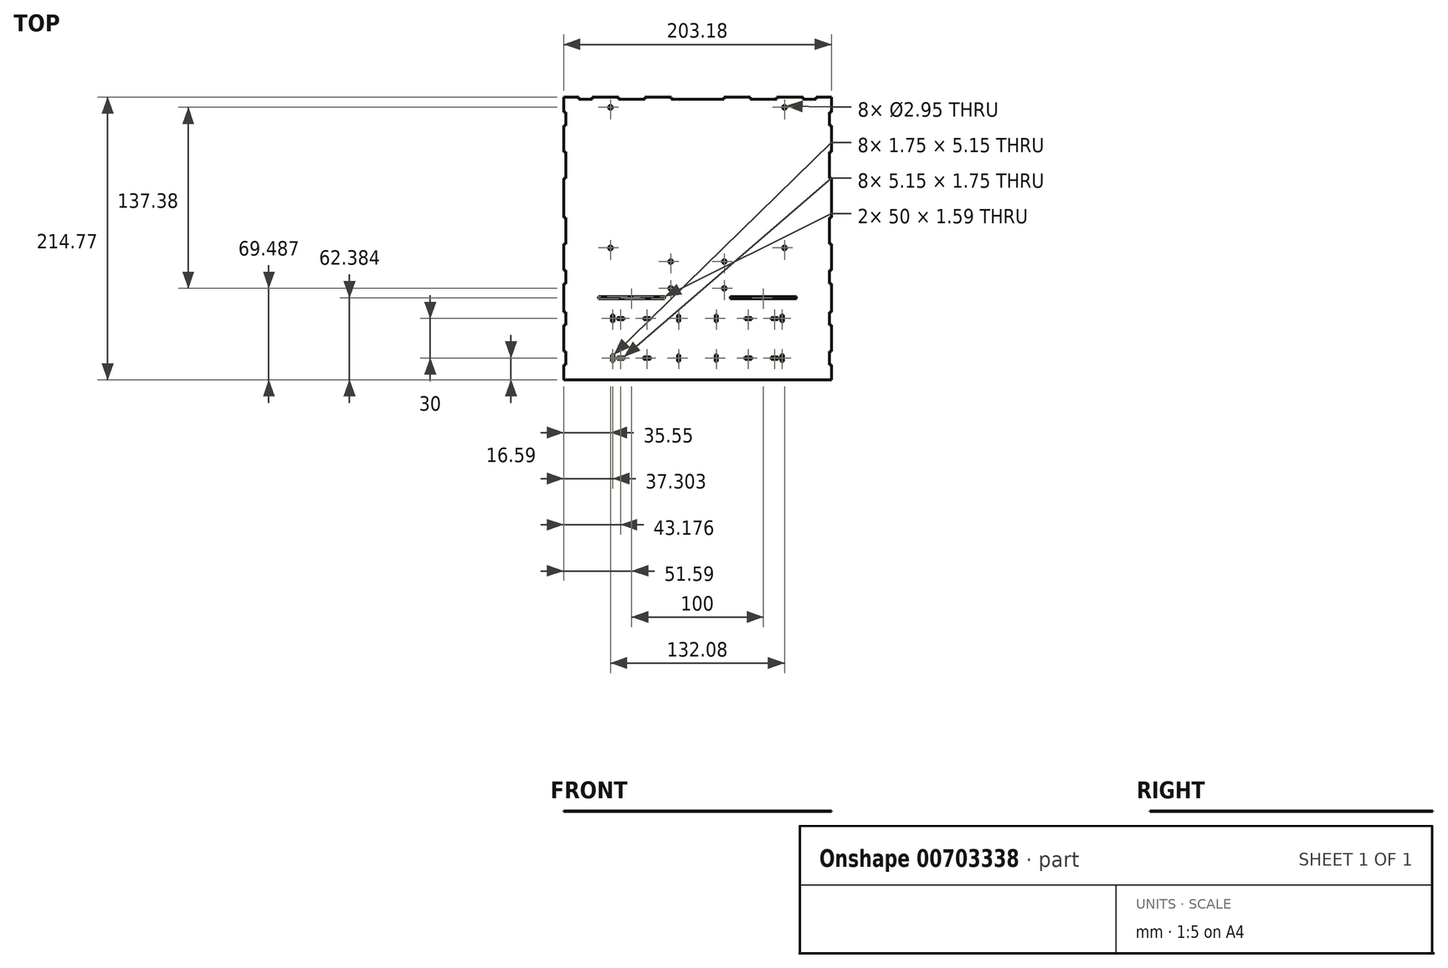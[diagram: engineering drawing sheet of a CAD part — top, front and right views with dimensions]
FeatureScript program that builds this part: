
annotation { "Feature Type Name" : "Feature", "Feature Type Description" : "" }
export const myFeature = defineFeature(function(context is Context, id is Id, definition is map)
    precondition{}
    {
        {
            var Q0;
            Q0=qCreatedBy(makeId("Top.planeOp"),FACE);
            var sketch = newSketch(context, id + "F0", { "sketchPlane" : qUnion([Q0])});
            skLineSegment(sketch, "E0.bottom", {"start": v(100, 20) * mm, "end": v(-100, 20) * mm});
            skLineSegment(sketch, "E0.top", {"start": v(100, -20) * mm, "end": v(-100, -20) * mm});
            skLineSegment(sketch, "E0.left", {"start": v(100, 20) * mm, "end": v(100, -20) * mm});
            skLineSegment(sketch, "E0.right", {"start": v(-100, 20) * mm, "end": v(-100, -20) * mm});
            skPoint(sketch, "E0.middle", {"position": v(0, 0) * mm});
            skLineSegment(sketch, "E1.bottom", {"start": v(-13.41, 12.42) * mm, "end": v(-15.16, 12.42) * mm});
            skLineSegment(sketch, "E1.top", {"start": v(-13.41, 17.57) * mm, "end": v(-15.16, 17.57) * mm});
            skLineSegment(sketch, "E1.left", {"start": v(-13.41, 12.42) * mm, "end": v(-13.41, 17.57) * mm});
            skLineSegment(sketch, "E1.right", {"start": v(-15.16, 12.42) * mm, "end": v(-15.16, 17.57) * mm});
            skPoint(sketch, "E1.middle", {"position": v(-14.29, 15) * mm});
            skPoint(sketch, "E2.cornerSnap0", {"position": v(-13.41, 15) * mm});
            skLineSegment(sketch, "E3.bottom", {"start": v(15.16, 12.42) * mm, "end": v(13.41, 12.42) * mm});
            skLineSegment(sketch, "E3.top", {"start": v(15.16, 17.57) * mm, "end": v(13.41, 17.57) * mm});
            skLineSegment(sketch, "E3.left", {"start": v(15.16, 12.42) * mm, "end": v(15.16, 17.57) * mm});
            skLineSegment(sketch, "E3.right", {"start": v(13.41, 12.42) * mm, "end": v(13.41, 17.57) * mm});
            skPoint(sketch, "E3.middle", {"position": v(14.29, 15) * mm});
            skLineSegment(sketch, "E4.bottom", {"start": v(15.16, -12.43) * mm, "end": v(13.41, -12.43) * mm});
            skLineSegment(sketch, "E4.top", {"start": v(15.16, -17.57) * mm, "end": v(13.41, -17.57) * mm});
            skLineSegment(sketch, "E4.left", {"start": v(15.16, -12.43) * mm, "end": v(15.16, -17.57) * mm});
            skLineSegment(sketch, "E4.right", {"start": v(13.41, -12.43) * mm, "end": v(13.41, -17.57) * mm});
            skPoint(sketch, "E4.middle", {"position": v(14.29, -15) * mm});
            skLineSegment(sketch, "E5.bottom", {"start": v(-13.41, -12.43) * mm, "end": v(-15.16, -12.43) * mm});
            skLineSegment(sketch, "E5.top", {"start": v(-13.41, -17.57) * mm, "end": v(-15.16, -17.57) * mm});
            skLineSegment(sketch, "E5.left", {"start": v(-13.41, -12.43) * mm, "end": v(-13.41, -17.57) * mm});
            skLineSegment(sketch, "E5.right", {"start": v(-15.16, -12.43) * mm, "end": v(-15.16, -17.57) * mm});
            skPoint(sketch, "E5.middle", {"position": v(-14.29, -15) * mm});
            skLineSegment(sketch, "E6.bottom", {"start": v(-63.41, 12.42) * mm, "end": v(-65.16, 12.42) * mm});
            skLineSegment(sketch, "E6.top", {"start": v(-63.41, 17.57) * mm, "end": v(-65.16, 17.57) * mm});
            skLineSegment(sketch, "E6.left", {"start": v(-63.41, 12.42) * mm, "end": v(-63.41, 17.57) * mm});
            skLineSegment(sketch, "E6.right", {"start": v(-65.16, 12.42) * mm, "end": v(-65.16, 17.57) * mm});
            skPoint(sketch, "E6.middle", {"position": v(-64.29, 15) * mm});
            skPoint(sketch, "E7.cornerSnap0", {"position": v(-63.41, 15) * mm});
            skLineSegment(sketch, "E8.bottom", {"start": v(-63.41, -17.57) * mm, "end": v(-65.16, -17.57) * mm});
            skLineSegment(sketch, "E8.top", {"start": v(-63.41, -12.42) * mm, "end": v(-65.16, -12.42) * mm});
            skLineSegment(sketch, "E8.left", {"start": v(-63.41, -17.58) * mm, "end": v(-63.41, -12.43) * mm});
            skLineSegment(sketch, "E8.right", {"start": v(-65.16, -17.58) * mm, "end": v(-65.16, -12.43) * mm});
            skPoint(sketch, "E8.middle", {"position": v(-64.29, -15) * mm});
            skPoint(sketch, "E9.cornerSnap0", {"position": v(-63.41, -15) * mm});
            skLineSegment(sketch, "E10.bottom", {"start": v(65.16, -17.57) * mm, "end": v(63.41, -17.57) * mm});
            skLineSegment(sketch, "E10.top", {"start": v(65.16, -12.43) * mm, "end": v(63.41, -12.43) * mm});
            skLineSegment(sketch, "E10.left", {"start": v(65.16, -17.58) * mm, "end": v(65.16, -12.43) * mm});
            skLineSegment(sketch, "E10.right", {"start": v(63.41, -17.58) * mm, "end": v(63.41, -12.43) * mm});
            skPoint(sketch, "E10.middle", {"position": v(64.29, -15) * mm});
            skPoint(sketch, "E11.cornerSnap0", {"position": v(65.16, -15) * mm});
            skLineSegment(sketch, "E12.bottom", {"start": v(65.16, 12.43) * mm, "end": v(63.41, 12.43) * mm});
            skLineSegment(sketch, "E12.top", {"start": v(65.16, 17.57) * mm, "end": v(63.41, 17.57) * mm});
            skLineSegment(sketch, "E12.left", {"start": v(65.16, 12.43) * mm, "end": v(65.16, 17.58) * mm});
            skLineSegment(sketch, "E12.right", {"start": v(63.41, 12.43) * mm, "end": v(63.41, 17.57) * mm});
            skPoint(sketch, "E12.middle", {"position": v(64.29, 15) * mm});
            skPoint(sketch, "E13.cornerSnap0", {"position": v(65.16, 15) * mm});
            skLineSegment(sketch, "E14.bottom", {"start": v(-55.84, -15.87) * mm, "end": v(-60.99, -15.87) * mm});
            skLineSegment(sketch, "E14.top", {"start": v(-55.84, -14.13) * mm, "end": v(-60.99, -14.13) * mm});
            skLineSegment(sketch, "E14.left", {"start": v(-55.84, -15.87) * mm, "end": v(-55.84, -14.13) * mm});
            skLineSegment(sketch, "E14.right", {"start": v(-60.99, -15.87) * mm, "end": v(-60.99, -14.13) * mm});
            skPoint(sketch, "E14.middle", {"position": v(-58.41, -15) * mm});
            skLineSegment(sketch, "E15.bottom", {"start": v(60.99, -15.87) * mm, "end": v(55.84, -15.87) * mm});
            skLineSegment(sketch, "E15.top", {"start": v(60.99, -14.13) * mm, "end": v(55.84, -14.13) * mm});
            skLineSegment(sketch, "E15.left", {"start": v(60.99, -15.87) * mm, "end": v(60.99, -14.13) * mm});
            skLineSegment(sketch, "E15.right", {"start": v(55.84, -15.87) * mm, "end": v(55.84, -14.13) * mm});
            skPoint(sketch, "E15.middle", {"position": v(58.41, -15) * mm});
            skLineSegment(sketch, "E16.bottom", {"start": v(60.99, 14.13) * mm, "end": v(55.84, 14.13) * mm});
            skLineSegment(sketch, "E16.top", {"start": v(60.99, 15.87) * mm, "end": v(55.84, 15.87) * mm});
            skLineSegment(sketch, "E16.left", {"start": v(60.99, 14.13) * mm, "end": v(60.99, 15.87) * mm});
            skLineSegment(sketch, "E16.right", {"start": v(55.84, 14.13) * mm, "end": v(55.84, 15.87) * mm});
            skPoint(sketch, "E16.middle", {"position": v(58.41, 15) * mm});
            skLineSegment(sketch, "E17.bottom", {"start": v(-55.84, 14.13) * mm, "end": v(-60.99, 14.13) * mm});
            skLineSegment(sketch, "E17.top", {"start": v(-55.84, 15.87) * mm, "end": v(-60.99, 15.87) * mm});
            skLineSegment(sketch, "E17.left", {"start": v(-55.84, 14.13) * mm, "end": v(-55.84, 15.87) * mm});
            skLineSegment(sketch, "E17.right", {"start": v(-60.99, 14.13) * mm, "end": v(-60.99, 15.87) * mm});
            skPoint(sketch, "E17.middle", {"position": v(-58.41, 15) * mm});
            skLineSegment(sketch, "E18.bottom", {"start": v(-35.84, 14.13) * mm, "end": v(-40.99, 14.13) * mm});
            skLineSegment(sketch, "E18.top", {"start": v(-35.84, 15.87) * mm, "end": v(-40.99, 15.87) * mm});
            skLineSegment(sketch, "E18.left", {"start": v(-35.84, 14.13) * mm, "end": v(-35.84, 15.87) * mm});
            skLineSegment(sketch, "E18.right", {"start": v(-40.99, 14.13) * mm, "end": v(-40.99, 15.87) * mm});
            skPoint(sketch, "E18.middle", {"position": v(-38.41, 15) * mm});
            skLineSegment(sketch, "E19.bottom", {"start": v(40.99, 14.13) * mm, "end": v(35.84, 14.13) * mm});
            skLineSegment(sketch, "E19.top", {"start": v(40.99, 15.87) * mm, "end": v(35.84, 15.87) * mm});
            skLineSegment(sketch, "E19.left", {"start": v(40.99, 14.13) * mm, "end": v(40.99, 15.87) * mm});
            skLineSegment(sketch, "E19.right", {"start": v(35.84, 14.13) * mm, "end": v(35.84, 15.87) * mm});
            skPoint(sketch, "E19.middle", {"position": v(38.41, 15) * mm});
            skLineSegment(sketch, "E20.bottom", {"start": v(-35.84, -15.87) * mm, "end": v(-40.99, -15.87) * mm});
            skLineSegment(sketch, "E20.top", {"start": v(-35.84, -14.13) * mm, "end": v(-40.99, -14.13) * mm});
            skLineSegment(sketch, "E20.left", {"start": v(-35.84, -15.87) * mm, "end": v(-35.84, -14.13) * mm});
            skLineSegment(sketch, "E20.right", {"start": v(-40.99, -15.87) * mm, "end": v(-40.99, -14.13) * mm});
            skPoint(sketch, "E20.middle", {"position": v(-38.41, -15) * mm});
            skLineSegment(sketch, "E21.bottom", {"start": v(40.99, -15.87) * mm, "end": v(35.84, -15.87) * mm});
            skLineSegment(sketch, "E21.top", {"start": v(40.99, -14.13) * mm, "end": v(35.84, -14.13) * mm});
            skLineSegment(sketch, "E21.left", {"start": v(40.99, -15.87) * mm, "end": v(40.99, -14.13) * mm});
            skLineSegment(sketch, "E21.right", {"start": v(35.84, -15.87) * mm, "end": v(35.84, -14.13) * mm});
            skPoint(sketch, "E21.middle", {"position": v(38.41, -15) * mm});
            skLineSegment(sketch, "E22", {"start": v(100, 20) * mm, "end": v(100, 30) * mm});
            skLineSegment(sketch, "E23", {"start": v(100, 30) * mm, "end": v(-100, 30) * mm});
            skLineSegment(sketch, "E24", {"start": v(-100, 30) * mm, "end": v(-100, 20) * mm});
            skLineSegment(sketch, "E25", {"start": v(-100, -20) * mm, "end": v(-100, -30) * mm});
            skLineSegment(sketch, "E26", {"start": v(-100, -30) * mm, "end": v(100, -30) * mm});
            skLineSegment(sketch, "E27", {"start": v(100, -30) * mm, "end": v(100, -20) * mm});
            skLineSegment(sketch, "E28", {"start": v(-100, 10) * mm, "end": v(-101.59, 10) * mm});
            skLineSegment(sketch, "E29", {"start": v(-101.59, 10) * mm, "end": v(-101.59, -10) * mm});
            skLineSegment(sketch, "E30", {"start": v(-101.59, -10) * mm, "end": v(-100, -10) * mm});
            skLineSegment(sketch, "E31", {"start": v(100, 10) * mm, "end": v(101.59, 10) * mm});
            skLineSegment(sketch, "E32", {"start": v(101.59, 10) * mm, "end": v(101.59, -10) * mm});
            skLineSegment(sketch, "E33", {"start": v(101.59, -10) * mm, "end": v(100, -10) * mm});
            skLineSegment(sketch, "E34", {"start": v(-100, 20) * mm, "end": v(-101.59, 20) * mm});
            skLineSegment(sketch, "E35", {"start": v(-101.59, 20) * mm, "end": v(-101.59, 30) * mm});
            skLineSegment(sketch, "E36", {"start": v(-101.59, 30) * mm, "end": v(-100, 30) * mm});
            skLineSegment(sketch, "E37", {"start": v(-100, -20) * mm, "end": v(-101.59, -20) * mm});
            skLineSegment(sketch, "E38", {"start": v(-101.59, -20) * mm, "end": v(-101.59, -30) * mm});
            skLineSegment(sketch, "E39", {"start": v(-101.59, -30) * mm, "end": v(-100, -30) * mm});
            skLineSegment(sketch, "E40", {"start": v(100, -20) * mm, "end": v(101.59, -20) * mm});
            skLineSegment(sketch, "E41", {"start": v(101.59, -20) * mm, "end": v(101.59, -30) * mm});
            skLineSegment(sketch, "E42", {"start": v(101.59, -30) * mm, "end": v(100, -30) * mm});
            skLineSegment(sketch, "E43", {"start": v(100, 30) * mm, "end": v(101.59, 30) * mm});
            skLineSegment(sketch, "E44", {"start": v(101.59, 30) * mm, "end": v(101.59, 20) * mm});
            skLineSegment(sketch, "E45", {"start": v(101.59, 20) * mm, "end": v(100, 20) * mm});
            skLineSegment(sketch, "E46", {"start": v(-101.59, 30) * mm, "end": v(-101.59, 31.59) * mm});
            skLineSegment(sketch, "E47", {"start": v(-101.59, 31.59) * mm, "end": v(101.59, 31.59) * mm});
            skLineSegment(sketch, "E48", {"start": v(101.59, 31.59) * mm, "end": v(101.59, 30) * mm});
            skLineSegment(sketch, "E49", {"start": v(101.59, -30) * mm, "end": v(101.59, -31.59) * mm});
            skLineSegment(sketch, "E50", {"start": v(101.59, -31.59) * mm, "end": v(-100, -31.59) * mm});
            skLineSegment(sketch, "E51", {"start": v(-100, -31.59) * mm, "end": v(-100, -30) * mm});
            skLineSegment(sketch, "E52", {"start": v(-75, 31.59) * mm, "end": v(-75, 30) * mm});
            skLineSegment(sketch, "E53", {"start": v(-25, 31.59) * mm, "end": v(-25, 30) * mm});
            skLineSegment(sketch, "E54", {"start": v(25, 31.59) * mm, "end": v(25, 30) * mm});
            skLineSegment(sketch, "E55", {"start": v(75, 31.59) * mm, "end": v(75, 30) * mm});
            skLineSegment(sketch, "E56", {"start": v(-101.59, -30) * mm, "end": v(-101.59, -31.59) * mm});
            skLineSegment(sketch, "E57", {"start": v(-101.59, -31.59) * mm, "end": v(-100, -31.59) * mm});
            skLineSegment(sketch, "E58", {"start": v(-101.59, 31.59) * mm, "end": v(-101.59, 181.59) * mm});
            skLineSegment(sketch, "E59", {"start": v(-101.59, 181.59) * mm, "end": v(101.59, 181.59) * mm});
            skLineSegment(sketch, "E60", {"start": v(101.59, 181.59) * mm, "end": v(101.59, 31.59) * mm});
            skLineSegment(sketch, "E61", {"start": v(-100, 30) * mm, "end": v(-100, 181.59) * mm});
            skLineSegment(sketch, "E62", {"start": v(100, 30) * mm, "end": v(100, 181.59) * mm});
            skLineSegment(sketch, "E63", {"start": v(101.59, 41.59) * mm, "end": v(100, 41.59) * mm});
            skLineSegment(sketch, "E64", {"start": v(100, 51.59) * mm, "end": v(101.59, 51.59) * mm});
            skLineSegment(sketch, "E65", {"start": v(101.59, 171.59) * mm, "end": v(100, 171.59) * mm});
            skLineSegment(sketch, "E66", {"start": v(101.59, 161.59) * mm, "end": v(100, 161.59) * mm});
            skLineSegment(sketch, "E67", {"start": v(-100, 41.59) * mm, "end": v(-101.59, 41.59) * mm});
            skLineSegment(sketch, "E68", {"start": v(-100, 51.59) * mm, "end": v(-101.59, 51.59) * mm});
            skLineSegment(sketch, "E69", {"start": v(-100, 171.59) * mm, "end": v(-101.59, 171.59) * mm});
            skLineSegment(sketch, "E70", {"start": v(-100, 161.59) * mm, "end": v(-101.59, 161.59) * mm});
            skLineSegment(sketch, "E71", {"start": v(101.59, 141.59) * mm, "end": v(100, 141.59) * mm});
            skLineSegment(sketch, "E72", {"start": v(101.59, 121.59) * mm, "end": v(100, 121.59) * mm});
            skLineSegment(sketch, "E73", {"start": v(101.59, 71.59) * mm, "end": v(100, 71.59) * mm});
            skLineSegment(sketch, "E74", {"start": v(101.59, 91.59) * mm, "end": v(100, 91.59) * mm});
            skLineSegment(sketch, "E75", {"start": v(-100, 141.59) * mm, "end": v(-101.59, 141.59) * mm});
            skLineSegment(sketch, "E76", {"start": v(-100, 121.59) * mm, "end": v(-101.59, 121.59) * mm});
            skLineSegment(sketch, "E77", {"start": v(-100, 71.59) * mm, "end": v(-101.59, 71.59) * mm});
            skLineSegment(sketch, "E78", {"start": v(-100, 91.59) * mm, "end": v(-101.59, 91.59) * mm});
            skCircle(sketch, "E79", {"center": v(-66.04, 175.28) * mm, "radius": 1.47 * mm});
            skCircle(sketch, "E80", {"center": v(66.04, 175.28) * mm, "radius": 1.47 * mm});
            skCircle(sketch, "E81", {"center": v(-66.04, 68.6) * mm, "radius": 1.47 * mm});
            skCircle(sketch, "E82", {"center": v(66.04, 68.6) * mm, "radius": 1.47 * mm});
            skLineSegment(sketch, "E83", {"start": v(-101.59, 181.59) * mm, "end": v(-101.59, 183.18) * mm});
            skLineSegment(sketch, "E84", {"start": v(-101.59, 183.18) * mm, "end": v(101.59, 183.18) * mm});
            skLineSegment(sketch, "E85", {"start": v(101.59, 183.18) * mm, "end": v(101.59, 181.59) * mm});
            skLineSegment(sketch, "E86", {"start": v(100, 181.59) * mm, "end": v(100, 183.18) * mm});
            skLineSegment(sketch, "E87", {"start": v(-100, 181.59) * mm, "end": v(-100, 183.18) * mm});
            skLineSegment(sketch, "E88", {"start": v(-90, 181.59) * mm, "end": v(-90, 183.18) * mm});
            skLineSegment(sketch, "E89", {"start": v(-80, 183.17) * mm, "end": v(-80, 181.59) * mm});
            skLineSegment(sketch, "E90", {"start": v(-60, 181.59) * mm, "end": v(-60, 183.17) * mm});
            skLineSegment(sketch, "E91", {"start": v(-40, 181.59) * mm, "end": v(-40, 183.17) * mm});
            skLineSegment(sketch, "E92", {"start": v(90, 183.18) * mm, "end": v(90, 181.59) * mm});
            skLineSegment(sketch, "E93", {"start": v(80, 183.18) * mm, "end": v(80, 181.59) * mm});
            skLineSegment(sketch, "E94", {"start": v(60, 183.18) * mm, "end": v(60, 181.59) * mm});
            skLineSegment(sketch, "E95", {"start": v(40, 183.18) * mm, "end": v(40, 181.59) * mm});
            skLineSegment(sketch, "E96", {"start": v(-20, 183.18) * mm, "end": v(-20, 181.59) * mm});
            skLineSegment(sketch, "E97", {"start": v(20, 183.18) * mm, "end": v(20, 181.59) * mm});
            skCircle(sketch, "E98", {"center": v(20.32, 58.22) * mm, "radius": 1.47 * mm});
            skCircle(sketch, "E99", {"center": v(20.32, 37.9) * mm, "radius": 1.47 * mm});
            skCircle(sketch, "E100", {"center": v(-20.32, 37.9) * mm, "radius": 1.47 * mm});
            skCircle(sketch, "E101", {"center": v(-20.32, 58.22) * mm, "radius": 1.47 * mm});
            skSolve(sketch);
        }
        {
            var Q0;
            {var subQ3=sQuery(id+"F0.wireOp",EDGE,"E69");Q0=makeQuery(id+"F0.imprint","IMPRINT",FACE,{"disambiguationData":[TD([[makeQuery(id+"F0.imprint","IMPRINT",EDGE,{"derivedFrom":subQ3}),-1.0]])]});}
            var Q1;
            {var subQ5=sQuery(id+"F0.wireOp",EDGE,"E67");Q1=makeQuery(id+"F0.imprint","IMPRINT",FACE,{"disambiguationData":[TD([[makeQuery(id+"F0.imprint","IMPRINT",EDGE,{"derivedFrom":subQ5}),1.0]])]});}
            var Q2;
            {var subQ0=sQuery(id+"F0.wireOp",EDGE,"E68");Q2=makeQuery(id+"F0.imprint","IMPRINT",FACE,{"disambiguationData":[TD([[makeQuery(id+"F0.imprint","IMPRINT",EDGE,{"derivedFrom":subQ0}),-1.0]])]});}
            var Q3;
            {var subQ5=sQuery(id+"F0.wireOp",EDGE,"E65");Q3=makeQuery(id+"F0.imprint","IMPRINT",FACE,{"disambiguationData":[TD([[makeQuery(id+"F0.imprint","IMPRINT",EDGE,{"derivedFrom":subQ5}),-1.0]])]});}
            var Q4;
            {var subQ5=sQuery(id+"F0.wireOp",EDGE,"E63");Q4=makeQuery(id+"F0.imprint","IMPRINT",FACE,{"disambiguationData":[TD([[makeQuery(id+"F0.imprint","IMPRINT",EDGE,{"derivedFrom":subQ5}),1.0]])]});}
            var Q5;
            {var subQ0=sQuery(id+"F0.wireOp",EDGE,"E64");Q5=makeQuery(id+"F0.imprint","IMPRINT",FACE,{"disambiguationData":[TD([[makeQuery(id+"F0.imprint","IMPRINT",EDGE,{"derivedFrom":subQ0}),1.0]])]});}
            var Q6;
            {var subQ4=sQuery(id+"F0.wireOp",EDGE,"E0.bottom");Q6=makeQuery(id+"F0.imprint","IMPRINT",FACE,{"disambiguationData":[TD([[makeQuery(id+"F0.imprint","IMPRINT",EDGE,{"derivedFrom":subQ4}),1.0]])]});}
            var Q7;
            Q7=makeQuery(id+"F0.imprint","IMPRINT",FACE,{"disambiguationData":[TD([[makeQuery(id+"F0.imprint","IMPRINT",EDGE,{"derivedFrom":sQuery(id+"F0.wireOp",EDGE,"E0.bottom")}),-1.0]])]});
            var Q8;
            Q8=makeQuery(id+"F0.imprint","IMPRINT",FACE,{"disambiguationData":[TD([[makeQuery(id+"F0.imprint","IMPRINT",EDGE,{"derivedFrom":sQuery(id+"F0.wireOp",EDGE,"E0.top")}),1.0]])]});
            var Q9;
            {var subQ0=sQuery(id+"F0.wireOp",EDGE,"E28");Q9=makeQuery(id+"F0.imprint","IMPRINT",FACE,{"disambiguationData":[TD([[makeQuery(id+"F0.imprint","IMPRINT",EDGE,{"derivedFrom":subQ0}),1.0]])]});}
            var Q10;
            {var subQ0=sQuery(id+"F0.wireOp",EDGE,"E31");Q10=makeQuery(id+"F0.imprint","IMPRINT",FACE,{"disambiguationData":[TD([[makeQuery(id+"F0.imprint","IMPRINT",EDGE,{"derivedFrom":subQ0}),-1.0]])]});}
            var Q11;
            Q11=makeQuery(id+"F0.imprint","IMPRINT",FACE,{"disambiguationData":[TD([[makeQuery(id+"F0.imprint","IMPRINT",EDGE,{"derivedFrom":sQuery(id+"F0.wireOp",EDGE,"E22")}),-1.0]])]});
            var Q12;
            Q12=makeQuery(id+"F0.imprint","IMPRINT",FACE,{"disambiguationData":[TD([[makeQuery(id+"F0.imprint","IMPRINT",EDGE,{"derivedFrom":sQuery(id+"F0.wireOp",EDGE,"E27")}),-1.0]])]});
            var Q13;
            Q13=makeQuery(id+"F0.imprint","IMPRINT",FACE,{"disambiguationData":[TD([[makeQuery(id+"F0.imprint","IMPRINT",EDGE,{"derivedFrom":sQuery(id+"F0.wireOp",EDGE,"E24")}),-1.0]])]});
            var Q14;
            Q14=makeQuery(id+"F0.imprint","IMPRINT",FACE,{"disambiguationData":[TD([[makeQuery(id+"F0.imprint","IMPRINT",EDGE,{"derivedFrom":sQuery(id+"F0.wireOp",EDGE,"E25")}),-1.0]])]});
            var Q15;
            Q15=makeQuery(id+"F0.imprint","IMPRINT",FACE,{"disambiguationData":[TD([[makeQuery(id+"F0.imprint","IMPRINT",EDGE,{"derivedFrom":sQuery(id+"F0.wireOp",EDGE,"E26")}),-1.0]])]});
            var Q16;
            {var subQ0=sQuery(id+"F0.wireOp",EDGE,"E36");Q16=makeQuery(id+"F0.imprint","IMPRINT",FACE,{"disambiguationData":[TD([[makeQuery(id+"F0.imprint","IMPRINT",EDGE,{"derivedFrom":subQ0}),1.0]])]});}
            var Q17;
            {var subQ0=sQuery(id+"F0.wireOp",EDGE,"E53");Q17=makeQuery(id+"F0.imprint","IMPRINT",FACE,{"disambiguationData":[TD([[makeQuery(id+"F0.imprint","IMPRINT",EDGE,{"derivedFrom":subQ0}),1.0]])]});}
            var Q18;
            {var subQ0=sQuery(id+"F0.wireOp",EDGE,"E43");Q18=makeQuery(id+"F0.imprint","IMPRINT",FACE,{"disambiguationData":[TD([[makeQuery(id+"F0.imprint","IMPRINT",EDGE,{"derivedFrom":subQ0}),1.0]])]});}
            var Q19;
            Q19=makeQuery(id+"F0.imprint","IMPRINT",FACE,{"disambiguationData":[TD([[makeQuery(id+"F0.imprint","IMPRINT",EDGE,{"derivedFrom":sQuery(id+"F0.wireOp",EDGE,"E39")}),-1.0]])]});
            var Q20;
            {var subQ4=sQuery(id+"F0.wireOp",EDGE,"E47");var subQ13=makeQuery(id+"F0.imprint","INTERSECT",VERTEX,{"derivedFrom":[subQ4,sQuery(id+"F0.wireOp",EDGE,"E52")]});Q20=makeQuery(id+"F0.imprint","IMPRINT",FACE,{"disambiguationData":[TD([[makeQuery(id+"F0.imprint","IMPRINT",EDGE,{"disambiguationData":[TD([[subQ13,1.0]])],"derivedFrom":subQ4}),1.0]])]});}
            var Q21;
            {var subQ3=sQuery(id+"F0.wireOp",EDGE,"E55");Q21=makeQuery(id+"F0.imprint","IMPRINT",FACE,{"disambiguationData":[TD([[makeQuery(id+"F0.imprint","IMPRINT",EDGE,{"derivedFrom":subQ3}),1.0]])]});}
            var Q22;
            {var subQ3=sQuery(id+"F0.wireOp",EDGE,"E52");Q22=makeQuery(id+"F0.imprint","IMPRINT",FACE,{"disambiguationData":[TD([[makeQuery(id+"F0.imprint","IMPRINT",EDGE,{"derivedFrom":subQ3}),-1.0]])]});}
            var Q23;
            {var subQ0=sQuery(id+"F0.wireOp",EDGE,"E76");Q23=makeQuery(id+"F0.imprint","IMPRINT",FACE,{"disambiguationData":[TD([[makeQuery(id+"F0.imprint","IMPRINT",EDGE,{"derivedFrom":subQ0}),1.0]])]});}
            var Q24;
            {var subQ0=sQuery(id+"F0.wireOp",EDGE,"E70");Q24=makeQuery(id+"F0.imprint","IMPRINT",FACE,{"disambiguationData":[TD([[makeQuery(id+"F0.imprint","IMPRINT",EDGE,{"derivedFrom":subQ0}),1.0]])]});}
            var Q25;
            {var subQ0=sQuery(id+"F0.wireOp",EDGE,"E66");Q25=makeQuery(id+"F0.imprint","IMPRINT",FACE,{"disambiguationData":[TD([[makeQuery(id+"F0.imprint","IMPRINT",EDGE,{"derivedFrom":subQ0}),1.0]])]});}
            var Q26;
            {var subQ0=sQuery(id+"F0.wireOp",EDGE,"E72");Q26=makeQuery(id+"F0.imprint","IMPRINT",FACE,{"disambiguationData":[TD([[makeQuery(id+"F0.imprint","IMPRINT",EDGE,{"derivedFrom":subQ0}),1.0]])]});}
            var Q27;
            {var subQ2=sQuery(id+"F0.wireOp",EDGE,"E86");Q27=makeQuery(id+"F0.imprint","IMPRINT",FACE,{"disambiguationData":[TD([[makeQuery(id+"F0.imprint","IMPRINT",EDGE,{"derivedFrom":subQ2}),1.0]])]});}
            var Q28;
            {var subQ0=sQuery(id+"F0.wireOp",EDGE,"E85");Q28=makeQuery(id+"F0.imprint","IMPRINT",FACE,{"disambiguationData":[TD([[makeQuery(id+"F0.imprint","IMPRINT",EDGE,{"derivedFrom":subQ0}),-1.0]])]});}
            var Q29;
            {var subQ0=sQuery(id+"F0.wireOp",EDGE,"E83");Q29=makeQuery(id+"F0.imprint","IMPRINT",FACE,{"disambiguationData":[TD([[makeQuery(id+"F0.imprint","IMPRINT",EDGE,{"derivedFrom":subQ0}),-1.0]])]});}
            var Q30;
            {var subQ0=sQuery(id+"F0.wireOp",EDGE,"E87");Q30=makeQuery(id+"F0.imprint","IMPRINT",FACE,{"disambiguationData":[TD([[makeQuery(id+"F0.imprint","IMPRINT",EDGE,{"derivedFrom":subQ0}),-1.0]])]});}
            var Q31;
            {var subQ0=sQuery(id+"F0.wireOp",EDGE,"E89");Q31=makeQuery(id+"F0.imprint","IMPRINT",FACE,{"disambiguationData":[TD([[makeQuery(id+"F0.imprint","IMPRINT",EDGE,{"derivedFrom":subQ0}),1.0]])]});}
            var Q32;
            {var subQ0=sQuery(id+"F0.wireOp",EDGE,"E91");Q32=makeQuery(id+"F0.imprint","IMPRINT",FACE,{"disambiguationData":[TD([[makeQuery(id+"F0.imprint","IMPRINT",EDGE,{"derivedFrom":subQ0}),-1.0]])]});}
            var Q33;
            {var subQ0=sQuery(id+"F0.wireOp",EDGE,"E93");Q33=makeQuery(id+"F0.imprint","IMPRINT",FACE,{"disambiguationData":[TD([[makeQuery(id+"F0.imprint","IMPRINT",EDGE,{"derivedFrom":subQ0}),-1.0]])]});}
            var Q34;
            {var subQ0=sQuery(id+"F0.wireOp",EDGE,"E95");Q34=makeQuery(id+"F0.imprint","IMPRINT",FACE,{"disambiguationData":[TD([[makeQuery(id+"F0.imprint","IMPRINT",EDGE,{"derivedFrom":subQ0}),-1.0]])]});}
            extrude(context, id + "F1", {"entities" : qUnion([Q0, Q1, Q2, Q3, Q4, Q5, Q6, Q7, Q8, Q9, Q10, Q11, Q12, Q13, Q14, Q15, Q16, Q17, Q18, Q19, Q20, Q21, Q22, Q23, Q24, Q25, Q26, Q27, Q28, Q29, Q30, Q31, Q32, Q33, Q34]), "depth" : 1 / 406.4 * mm, "offsetDistance" : 25 * mm});
        }
    });
